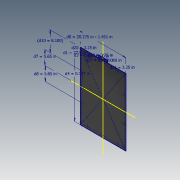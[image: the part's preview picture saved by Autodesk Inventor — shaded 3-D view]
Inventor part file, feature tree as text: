
AUTODESK INVENTOR PART (.ipt)
format: ipt  version: 2020.3 (Build 243373000, 373)  size: 132,608 bytes
history: native  units: in
note: dims shown in document units (in); Inventor stores cm internally (conversion verified against a paired STEP export)
features: fillet x2, sketch x1, extrude x1, hole x1
ambient origin geometry x8: Origin, YZ Plane, XZ Plane, XY Plane, X Axis, Y Axis, Z Axis, Center Point
bodies: Solid1 (feature_tree)
feature tree (5):
  sketch  "Sketch1"  dims[d0=18.824in d1=27.5in d3=0.737in d4=0.737in d7=5.65in d8=5.65in d10=8.1in d11=0.125in d12=0.0in d13=0.325in d14=0.75in d15=0.375in d16=0.25in d17=0.5635in d18=1.0in d19=0.8108in d20=3.25in d21=3.25in d22=0.375in d23=3.75in d24=1.0in d25=0.125in d27=0.487in]
  extrude  "Extrusion1"  Depth=27.5in
  hole  "Hole1"  [1 undecoded]
  fillet  "Fillet1"  Radius=0.737in
  fillet  "Fillet2"  Radius=5.65in
note: 1 required parameter value undecoded (feature->parameter linkage not recoverable at this tier; creation-order binding heuristic only, values carry confidence <= 0.55)
